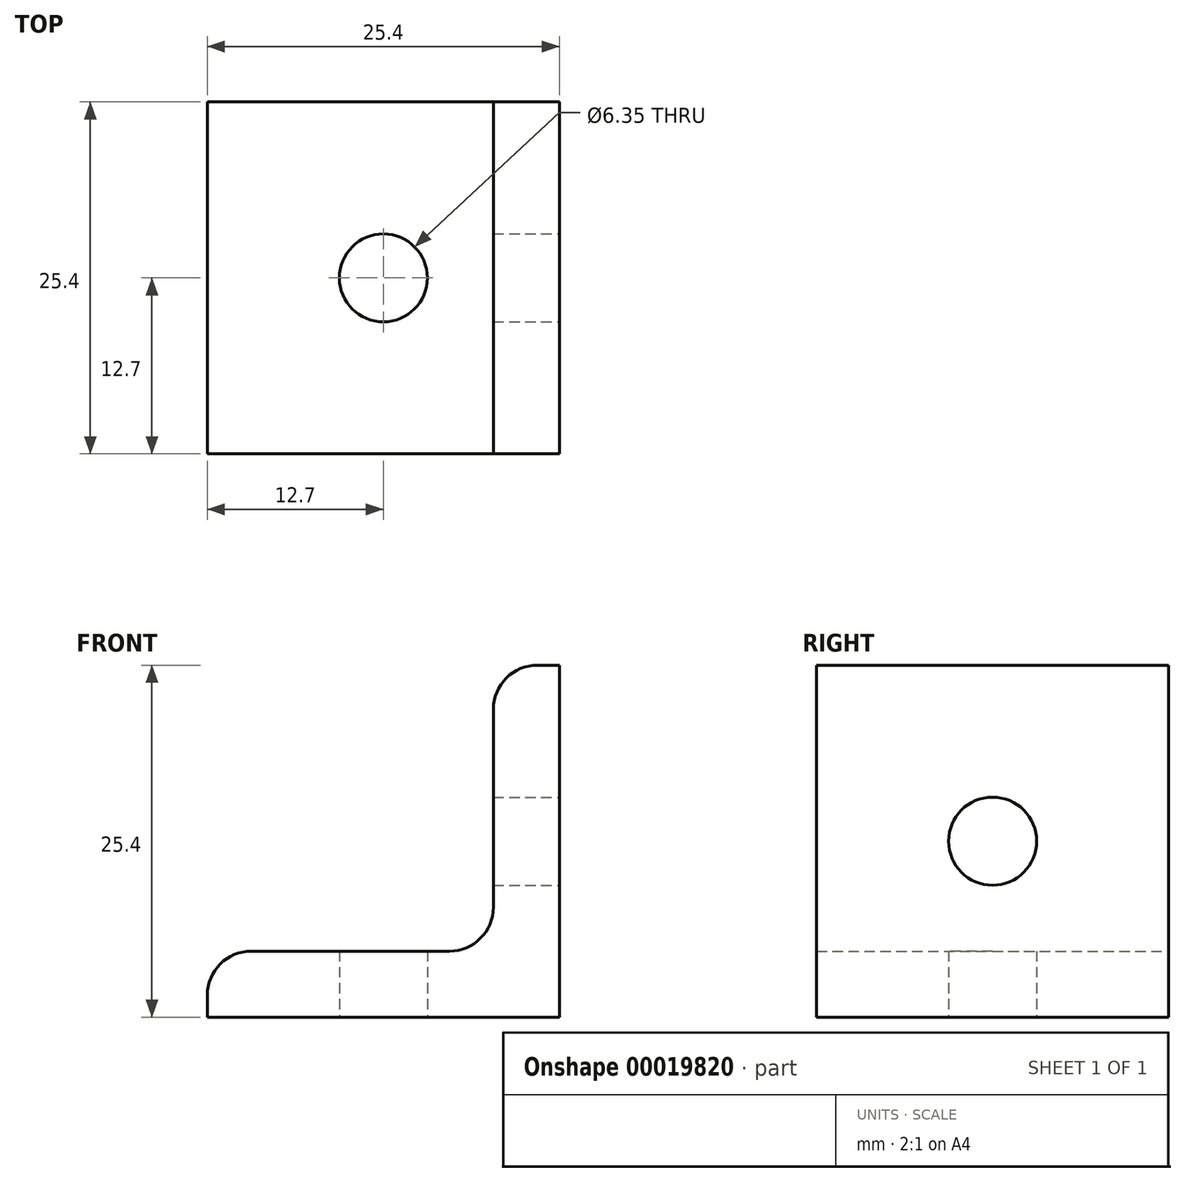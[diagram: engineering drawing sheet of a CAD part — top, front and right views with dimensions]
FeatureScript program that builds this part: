
annotation { "Feature Type Name" : "Feature", "Feature Type Description" : "" }
export const myFeature = defineFeature(function(context is Context, id is Id, definition is map)
    precondition{}
    {
        {
            var Q0;
            Q0=qCreatedBy(makeId("Front.planeOp"),FACE);
            var sketch = newSketch(context, id + "F0", { "sketchPlane" : qUnion([Q0])});
            skLineSegment(sketch, "E0.bottom", {"start": v(0, 0) * mm, "end": v(-25.4, 0) * mm});
            skLineSegment(sketch, "E0.top", {"start": v(0, 25.4) * mm, "end": v(-4.76, 25.4) * mm});
            skLineSegment(sketch, "E0.left", {"start": v(0, 0) * mm, "end": v(0, 25.4) * mm});
            skLineSegment(sketch, "E0.right", {"start": v(-25.4, 0) * mm, "end": v(-25.4, 4.76) * mm});
            skLineSegment(sketch, "E1.top", {"start": v(-25.4, 4.76) * mm, "end": v(-4.76, 4.76) * mm});
            skLineSegment(sketch, "E1.right", {"start": v(-4.76, 25.4) * mm, "end": v(-4.76, 4.76) * mm});
            skSolve(sketch);
        }
        {
            var Q0;
            Q0=makeQuery(id+"F0.imprint","IMPRINT",FACE,{"disambiguationData":[TD([[makeQuery(id+"F0.imprint","IMPRINT",EDGE,{"derivedFrom":sQuery(id+"F0.wireOp",EDGE,"E0.bottom")}),-1.0]])]});
            extrude(context, id + "F1", {"entities" : qUnion([Q0]), "endBound" : BoundingType.SYMMETRIC, "depth" : 25.4 * mm});
        }
        {
            var Q0;
            Q0=makeQuery(id+"F1.opExtrude","SWEPT_EDGE",EDGE,{"disambiguationData":[OSD([sQuery(id+"F0.wireOp",EDGE,"E0.top"),sQuery(id+"F0.wireOp",EDGE,"E1.right")])]});
            var Q1;
            Q1=makeQuery(id+"F1.opExtrude","SWEPT_EDGE",EDGE,{"disambiguationData":[OSD([sQuery(id+"F0.wireOp",EDGE,"E0.right"),sQuery(id+"F0.wireOp",EDGE,"E1.top")])]});
            fillet(context, id + "F2", {"entities" : qUnion([Q0, Q1]), "radius" : 3.17 * mm, "tangentPropagation" : true, "allowEdgeOverflow" : false});
        }
        {
            var Q0;
            Q0=makeQuery(id+"F1.opExtrude","SWEPT_FACE",FACE,{"disambiguationData":[OSD([sQuery(id+"F0.wireOp",EDGE,"E0.left")])]});
            var sketch = newSketch(context, id + "F3", { "sketchPlane" : qUnion([Q0])});
            skPoint(sketch, "E2", {"position": v(0, 12.7) * mm});
            skLineSegment(sketch, "E3", {"start": v(0, 0) * mm, "end": v(0, 12.7) * mm});
            skSolve(sketch);
        }
        {
            var Q0;
            Q0=sQuery(id+"F3.wireOp",VERTEX,"E2");
            var Q1;
            Q1=makeQuery(id+"F1.opExtrude","SWEPT_BODY",BODY,{"disambiguationData":[OSD([sQuery(id+"F0.wireOp",EDGE,"E0.bottom"),sQuery(id+"F0.wireOp",EDGE,"E0.top"),sQuery(id+"F0.wireOp",EDGE,"E0.left"),sQuery(id+"F0.wireOp",EDGE,"E0.right"),sQuery(id+"F0.wireOp",EDGE,"E1.top"),sQuery(id+"F0.wireOp",EDGE,"E1.right")])]});
            hole(context, id + "F4", {"style" : HoleStyle.SIMPLE, "holeDiameter" : 6.35 * mm, "endStyle" : HoleEndStyle.THROUGH, "locations" : qUnion([Q0]), "scope" : qUnion([Q1])});
        }
        {
            var Q0;
            Q0=makeQuery(id+"F1.opExtrude","SWEPT_FACE",FACE,{"disambiguationData":[OSD([sQuery(id+"F0.wireOp",EDGE,"E0.bottom")])]});
            var sketch = newSketch(context, id + "F5", { "sketchPlane" : qUnion([Q0])});
            skPoint(sketch, "E4", {"position": v(-12.7, 0) * mm});
            skLineSegment(sketch, "E5", {"start": v(0, 0) * mm, "end": v(-12.7, 0) * mm});
            skSolve(sketch);
        }
        {
            var Q0;
            Q0=sQuery(id+"F5.wireOp",VERTEX,"E4");
            var Q1;
            Q1=makeQuery(id+"F1.opExtrude","SWEPT_BODY",BODY,{"disambiguationData":[OSD([sQuery(id+"F0.wireOp",EDGE,"E0.bottom"),sQuery(id+"F0.wireOp",EDGE,"E0.top"),sQuery(id+"F0.wireOp",EDGE,"E0.left"),sQuery(id+"F0.wireOp",EDGE,"E0.right"),sQuery(id+"F0.wireOp",EDGE,"E1.top"),sQuery(id+"F0.wireOp",EDGE,"E1.right")])]});
            hole(context, id + "F6", {"style" : HoleStyle.SIMPLE, "holeDiameter" : 6.35 * mm, "endStyle" : HoleEndStyle.THROUGH, "locations" : qUnion([Q0]), "scope" : qUnion([Q1])});
        }
        {
            var Q0;
            Q0=makeQuery(id+"F1.opExtrude","SWEPT_EDGE",EDGE,{"disambiguationData":[OSD([sQuery(id+"F0.wireOp",EDGE,"E1.top"),sQuery(id+"F0.wireOp",EDGE,"E1.right")])]});
            fillet(context, id + "F7", {"entities" : qUnion([Q0]), "radius" : 3.17 * mm, "tangentPropagation" : true, "allowEdgeOverflow" : false});
        }
    });
